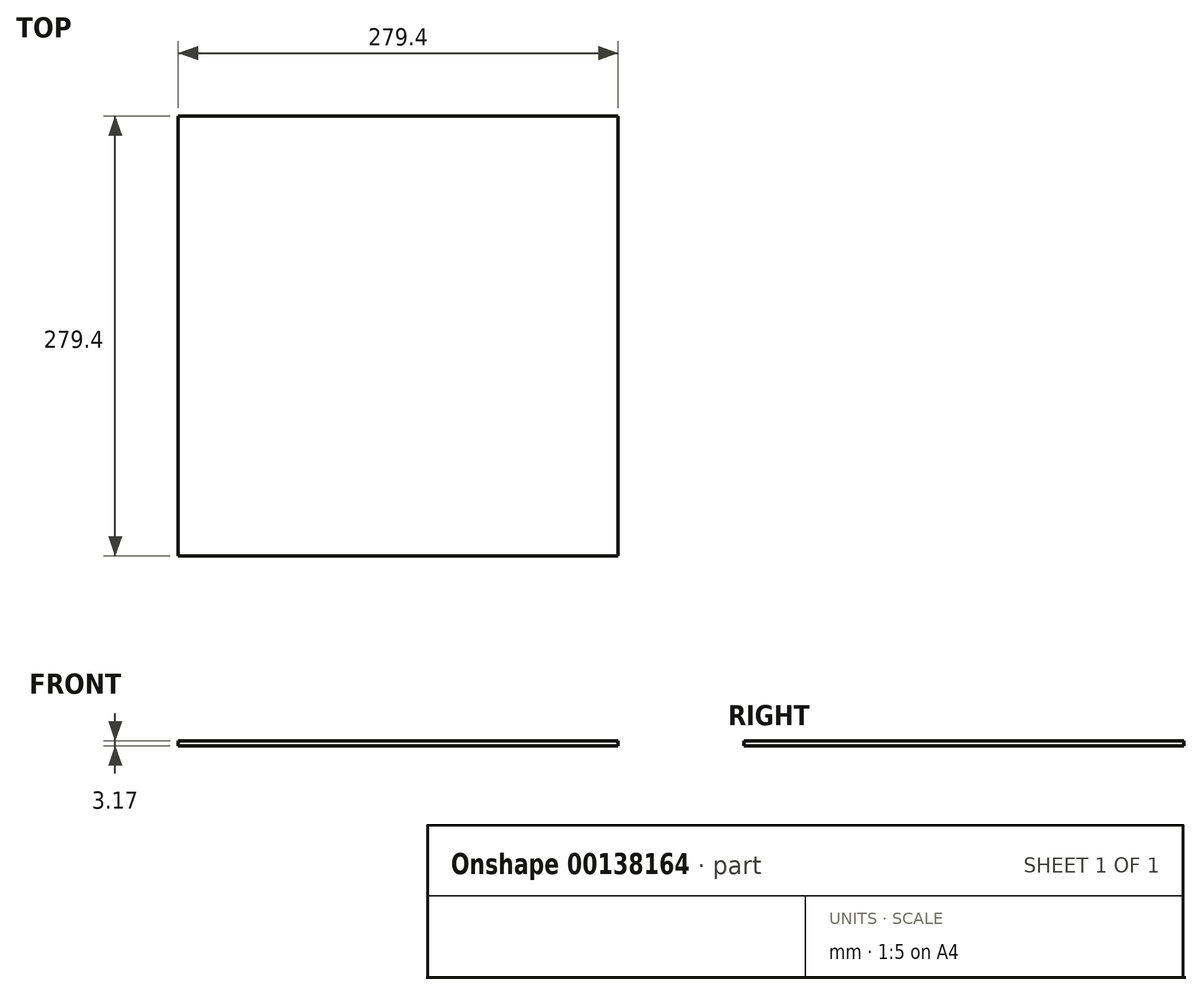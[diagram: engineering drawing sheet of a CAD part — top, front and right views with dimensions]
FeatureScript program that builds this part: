
annotation { "Feature Type Name" : "Feature", "Feature Type Description" : "" }
export const myFeature = defineFeature(function(context is Context, id is Id, definition is map)
    precondition{}
    {
        {
            var Q0;
            Q0=qCreatedBy(makeId("Top.planeOp"),FACE);
            var sketch = newSketch(context, id + "F0", { "sketchPlane" : qUnion([Q0])});
            skLineSegment(sketch, "E0.bottom", {"start": v(-140.55, 146.57) * mm, "end": v(138.85, 146.57) * mm});
            skLineSegment(sketch, "E0.top", {"start": v(-140.55, -132.83) * mm, "end": v(138.85, -132.83) * mm});
            skLineSegment(sketch, "E0.left", {"start": v(-140.55, 146.57) * mm, "end": v(-140.55, -132.83) * mm});
            skLineSegment(sketch, "E0.right", {"start": v(138.85, 146.57) * mm, "end": v(138.85, -132.83) * mm});
            skSolve(sketch);
        }
        {
            var Q0;
            Q0=makeQuery(id+"F0.imprint","IMPRINT",FACE,{"disambiguationData":[TD([[makeQuery(id+"F0.imprint","IMPRINT",EDGE,{"derivedFrom":sQuery(id+"F0.wireOp",EDGE,"E0.bottom")}),-1.0]])]});
            extrude(context, id + "F1", {"entities" : qUnion([Q0]), "depth" : 3.17 * mm});
        }
    });
